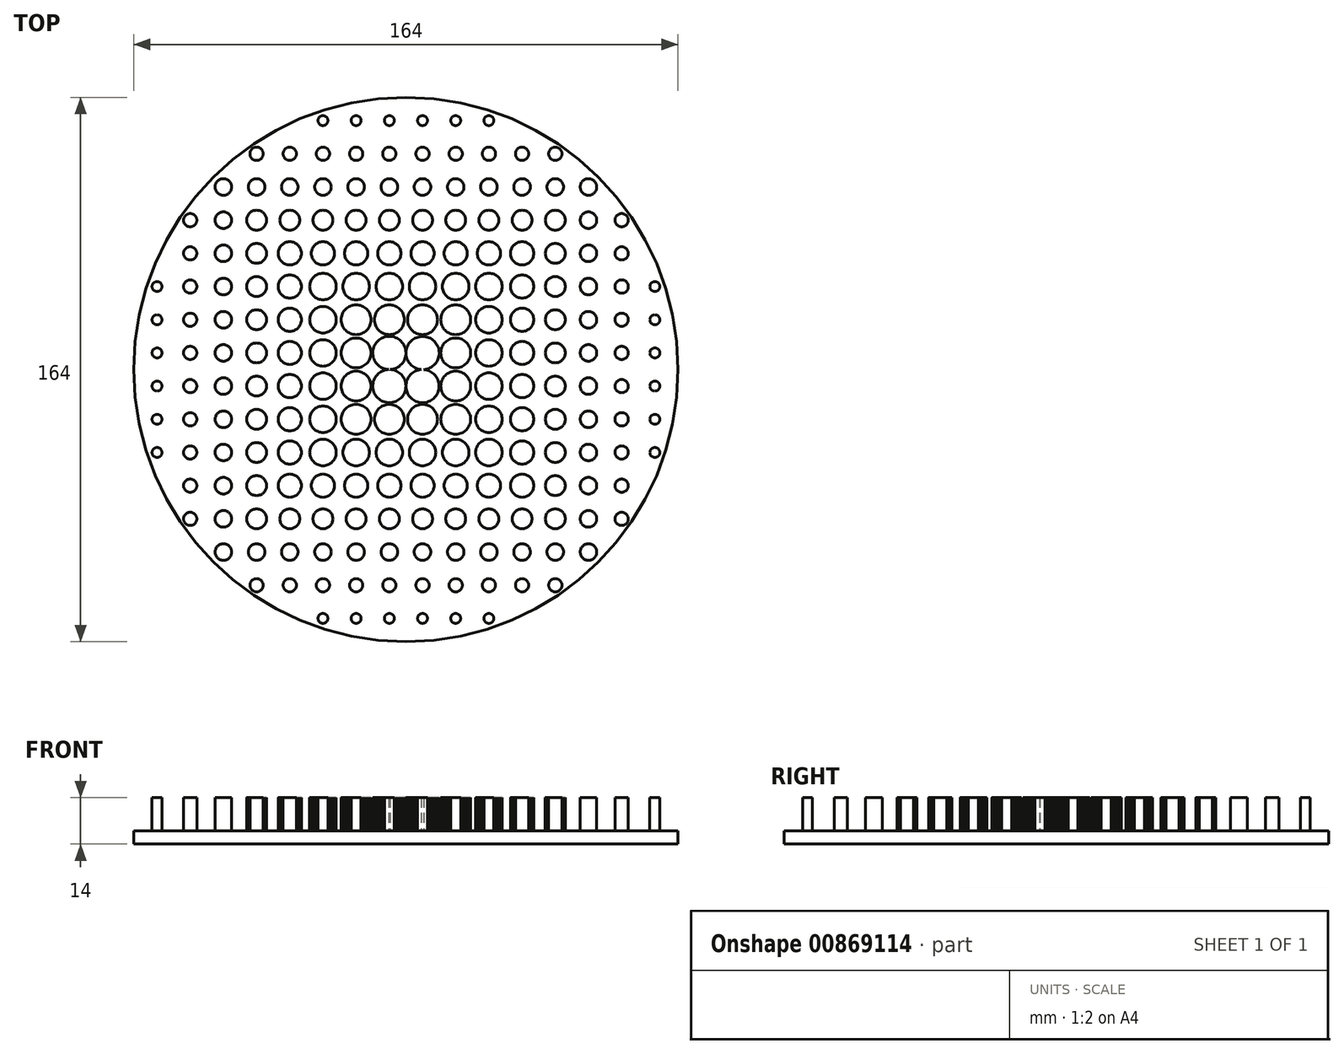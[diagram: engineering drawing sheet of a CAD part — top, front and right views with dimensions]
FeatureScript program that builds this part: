
annotation { "Feature Type Name" : "Feature", "Feature Type Description" : "" }
export const myFeature = defineFeature(function(context is Context, id is Id, definition is map)
    precondition{}
    {
        {
            var Q0;
            Q0=qCreatedBy(makeId("Top.planeOp"),FACE);
            var sketch = newSketch(context, id + "F0", { "sketchPlane" : qUnion([Q0])});
            skCircle(sketch, "E0", {"center": v(0, 0) * mm, "radius": 82 * mm});
            skSolve(sketch);
        }
        {
            var Q0;
            Q0=qSketchRegion(id+"F0",true);
            extrude(context, id + "F1", {"entities" : qUnion([Q0]), "oppositeDirection" : true, "depth" : 4 * mm, "offsetDistance" : 25 * mm});
        }
        {
            var Q0;
            Q0=makeQuery(id+"F1.opExtrude","CAP_FACE",FACE,{"disambiguationData":[OSD([sQuery(id+"F0.wireOp",EDGE,"E0")])],"isStart":true});
            var sketch = newSketch(context, id + "F2", { "sketchPlane" : qUnion([Q0])});
            skCircle(sketch, "E1", {"center": v(-5, 5) * mm, "radius": 5 * mm});
            skCircle(sketch, "E2", {"center": v(-5, 15) * mm, "radius": 4.5 * mm});
            skCircle(sketch, "E3.MirrorC", {"center": v(15, -5) * mm, "radius": 4.5 * mm});
            skCircle(sketch, "E4", {"center": v(5, 15) * mm, "radius": 4.5 * mm});
            skCircle(sketch, "E5.MirrorC", {"center": v(15, 5) * mm, "radius": 4.5 * mm});
            skCircle(sketch, "E6", {"center": v(15, 15) * mm, "radius": 4.5 * mm});
            skCircle(sketch, "E7", {"center": v(-15, 5) * mm, "radius": 4.5 * mm});
            skCircle(sketch, "E8", {"center": v(-15, -5) * mm, "radius": 4.5 * mm});
            skCircle(sketch, "E9.MirrorC", {"center": v(5, -15) * mm, "radius": 4.5 * mm});
            skCircle(sketch, "E10.MirrorC", {"center": v(-5, -15) * mm, "radius": 4.5 * mm});
            skCircle(sketch, "E11", {"center": v(-15, 15) * mm, "radius": 4.5 * mm});
            skCircle(sketch, "E12.MirrorC", {"center": v(15, -15) * mm, "radius": 4.5 * mm});
            skCircle(sketch, "E13", {"center": v(-15, -15) * mm, "radius": 4.5 * mm});
            skCircle(sketch, "E14", {"center": v(-15, 25) * mm, "radius": 4 * mm});
            skCircle(sketch, "E15.1.0.0", {"center": v(-5, 25) * mm, "radius": 4 * mm});
            skCircle(sketch, "E15.2.0.0", {"center": v(5, 25) * mm, "radius": 4 * mm});
            skCircle(sketch, "E15.3.0.0", {"center": v(15, 25) * mm, "radius": 4 * mm});
            skCircle(sketch, "E15.4.0.0", {"center": v(25, 25) * mm, "radius": 4 * mm});
            skLineSegment(sketch, "E15.direction1", {"start": v(-15, 25) * mm, "end": v(-5, 25) * mm, "construction": true});
            skCircle(sketch, "E16", {"center": v(-25, 25) * mm, "radius": 4 * mm});
            skCircle(sketch, "E17.MirrorC", {"center": v(25, 15) * mm, "radius": 4 * mm});
            skCircle(sketch, "E18.MirrorC", {"center": v(25, 5) * mm, "radius": 4 * mm});
            skCircle(sketch, "E19.MirrorC", {"center": v(25, -5) * mm, "radius": 4 * mm});
            skCircle(sketch, "E20.MirrorC", {"center": v(25, -15) * mm, "radius": 4 * mm});
            skCircle(sketch, "E21.MirrorC", {"center": v(25, -25) * mm, "radius": 4 * mm});
            skCircle(sketch, "E22.1.0.0", {"center": v(15, -25) * mm, "radius": 4 * mm});
            skCircle(sketch, "E22.2.0.0", {"center": v(5, -25) * mm, "radius": 4 * mm});
            skCircle(sketch, "E22.3.0.0", {"center": v(-5, -25) * mm, "radius": 4 * mm});
            skCircle(sketch, "E22.4.0.0", {"center": v(-15, -25) * mm, "radius": 4 * mm});
            skCircle(sketch, "E22.5.0.0", {"center": v(-25, -25) * mm, "radius": 4 * mm});
            skLineSegment(sketch, "E22.direction1", {"start": v(25, -25) * mm, "end": v(15, -25) * mm, "construction": true});
            skCircle(sketch, "E23.MirrorC", {"center": v(-25, 15) * mm, "radius": 4 * mm});
            skCircle(sketch, "E24.MirrorC", {"center": v(-25, 5) * mm, "radius": 4 * mm});
            skCircle(sketch, "E25.MirrorC", {"center": v(-25, -5) * mm, "radius": 4 * mm});
            skCircle(sketch, "E26.MirrorC", {"center": v(-25, -15) * mm, "radius": 4 * mm});
            skCircle(sketch, "E27", {"center": v(-25, 35) * mm, "radius": 3.5 * mm});
            skCircle(sketch, "E28.1.0.0", {"center": v(-15, 35) * mm, "radius": 3.5 * mm});
            skCircle(sketch, "E28.2.0.0", {"center": v(-5, 35) * mm, "radius": 3.5 * mm});
            skCircle(sketch, "E28.3.0.0", {"center": v(5, 35) * mm, "radius": 3.5 * mm});
            skCircle(sketch, "E28.4.0.0", {"center": v(15, 35) * mm, "radius": 3.5 * mm});
            skCircle(sketch, "E28.5.0.0", {"center": v(25, 35) * mm, "radius": 3.5 * mm});
            skCircle(sketch, "E28.6.0.0", {"center": v(35, 35) * mm, "radius": 3.5 * mm});
            skLineSegment(sketch, "E28.direction1", {"start": v(-25, 35) * mm, "end": v(-15, 35) * mm, "construction": true});
            skCircle(sketch, "E29.MirrorC", {"center": v(35, -15) * mm, "radius": 3.5 * mm});
            skCircle(sketch, "E30.MirrorC", {"center": v(35, -5) * mm, "radius": 3.5 * mm});
            skCircle(sketch, "E31.MirrorC", {"center": v(35, 5) * mm, "radius": 3.5 * mm});
            skCircle(sketch, "E32.MirrorC", {"center": v(35, 15) * mm, "radius": 3.5 * mm});
            skCircle(sketch, "E33.MirrorC", {"center": v(35, 25) * mm, "radius": 3.5 * mm});
            skCircle(sketch, "E34.MirrorC", {"center": v(35, -25) * mm, "radius": 3.5 * mm});
            skCircle(sketch, "E35.MirrorC", {"center": v(35, -35) * mm, "radius": 3.5 * mm});
            skCircle(sketch, "E36.1.0.0", {"center": v(25, -35) * mm, "radius": 3.5 * mm});
            skCircle(sketch, "E36.2.0.0", {"center": v(15, -35) * mm, "radius": 3.5 * mm});
            skCircle(sketch, "E36.3.0.0", {"center": v(5, -35) * mm, "radius": 3.5 * mm});
            skCircle(sketch, "E36.4.0.0", {"center": v(-5, -35) * mm, "radius": 3.5 * mm});
            skCircle(sketch, "E36.5.0.0", {"center": v(-15, -35) * mm, "radius": 3.5 * mm});
            skCircle(sketch, "E36.6.0.0", {"center": v(-25, -35) * mm, "radius": 3.5 * mm});
            skCircle(sketch, "E36.7.0.0", {"center": v(-35, -35) * mm, "radius": 3.5 * mm});
            skLineSegment(sketch, "E36.direction1", {"start": v(35, -35) * mm, "end": v(25, -35) * mm, "construction": true});
            skCircle(sketch, "E37.MirrorC", {"center": v(-35, -25) * mm, "radius": 3.5 * mm});
            skCircle(sketch, "E38.MirrorC", {"center": v(-35, -15) * mm, "radius": 3.5 * mm});
            skCircle(sketch, "E39.MirrorC", {"center": v(-35, -5) * mm, "radius": 3.5 * mm});
            skCircle(sketch, "E40.MirrorC", {"center": v(-35, 5) * mm, "radius": 3.5 * mm});
            skCircle(sketch, "E41.MirrorC", {"center": v(-35, 15) * mm, "radius": 3.5 * mm});
            skCircle(sketch, "E42.MirrorC", {"center": v(-35, 25) * mm, "radius": 3.5 * mm});
            skCircle(sketch, "E43.MirrorC", {"center": v(-35, 35) * mm, "radius": 3.5 * mm});
            skCircle(sketch, "E44", {"center": v(-35, 45) * mm, "radius": 3 * mm});
            skCircle(sketch, "E45.1.0.0", {"center": v(-25, 45) * mm, "radius": 3 * mm});
            skCircle(sketch, "E45.2.0.0", {"center": v(-15, 45) * mm, "radius": 3 * mm});
            skCircle(sketch, "E45.3.0.0", {"center": v(-5, 45) * mm, "radius": 3 * mm});
            skCircle(sketch, "E45.4.0.0", {"center": v(5, 45) * mm, "radius": 3 * mm});
            skCircle(sketch, "E45.5.0.0", {"center": v(15, 45) * mm, "radius": 3 * mm});
            skCircle(sketch, "E45.6.0.0", {"center": v(25, 45) * mm, "radius": 3 * mm});
            skCircle(sketch, "E45.7.0.0", {"center": v(35, 45) * mm, "radius": 3 * mm});
            skCircle(sketch, "E45.8.0.0", {"center": v(45, 45) * mm, "radius": 3 * mm});
            skLineSegment(sketch, "E45.direction1", {"start": v(-35, 45) * mm, "end": v(-25, 45) * mm, "construction": true});
            skCircle(sketch, "E46.MirrorC", {"center": v(45, -25) * mm, "radius": 3 * mm});
            skCircle(sketch, "E47.MirrorC", {"center": v(45, -35) * mm, "radius": 3 * mm});
            skCircle(sketch, "E48.MirrorC", {"center": v(45, -15) * mm, "radius": 3 * mm});
            skCircle(sketch, "E49.MirrorC", {"center": v(45, -5) * mm, "radius": 3 * mm});
            skCircle(sketch, "E50.MirrorC", {"center": v(45, 5) * mm, "radius": 3 * mm});
            skCircle(sketch, "E51.MirrorC", {"center": v(45, 15) * mm, "radius": 3 * mm});
            skCircle(sketch, "E52.MirrorC", {"center": v(45, 25) * mm, "radius": 3 * mm});
            skCircle(sketch, "E53.MirrorC", {"center": v(45, 35) * mm, "radius": 3 * mm});
            skCircle(sketch, "E54.MirrorC", {"center": v(45, -45) * mm, "radius": 3 * mm});
            skCircle(sketch, "E55.1.0.0", {"center": v(35, -45) * mm, "radius": 3 * mm});
            skCircle(sketch, "E55.2.0.0", {"center": v(25, -45) * mm, "radius": 3 * mm});
            skCircle(sketch, "E55.3.0.0", {"center": v(15, -45) * mm, "radius": 3 * mm});
            skCircle(sketch, "E55.4.0.0", {"center": v(5, -45) * mm, "radius": 3 * mm});
            skCircle(sketch, "E55.5.0.0", {"center": v(-5, -45) * mm, "radius": 3 * mm});
            skCircle(sketch, "E55.6.0.0", {"center": v(-15, -45) * mm, "radius": 3 * mm});
            skCircle(sketch, "E55.7.0.0", {"center": v(-25, -45) * mm, "radius": 3 * mm});
            skCircle(sketch, "E55.8.0.0", {"center": v(-35, -45) * mm, "radius": 3 * mm});
            skCircle(sketch, "E55.9.0.0", {"center": v(-45, -45) * mm, "radius": 3 * mm});
            skLineSegment(sketch, "E55.direction1", {"start": v(45, -45) * mm, "end": v(35, -45) * mm, "construction": true});
            skCircle(sketch, "E56.MirrorC", {"center": v(-45, -35) * mm, "radius": 3 * mm});
            skCircle(sketch, "E57.MirrorC", {"center": v(-45, -25) * mm, "radius": 3 * mm});
            skCircle(sketch, "E58.MirrorC", {"center": v(-45, -15) * mm, "radius": 3 * mm});
            skCircle(sketch, "E59.MirrorC", {"center": v(-45, -5) * mm, "radius": 3 * mm});
            skCircle(sketch, "E60.MirrorC", {"center": v(-45, 5) * mm, "radius": 3 * mm});
            skCircle(sketch, "E61.MirrorC", {"center": v(-45, 15) * mm, "radius": 3 * mm});
            skCircle(sketch, "E62.MirrorC", {"center": v(-45, 25) * mm, "radius": 3 * mm});
            skCircle(sketch, "E63.MirrorC", {"center": v(-45, 35) * mm, "radius": 3 * mm});
            skCircle(sketch, "E64.MirrorC", {"center": v(-45, 45) * mm, "radius": 3 * mm});
            skCircle(sketch, "E65", {"center": v(-45, 55) * mm, "radius": 2.5 * mm});
            skCircle(sketch, "E66.1.0.0", {"center": v(-35, 55) * mm, "radius": 2.5 * mm});
            skCircle(sketch, "E66.2.0.0", {"center": v(-25, 55) * mm, "radius": 2.5 * mm});
            skCircle(sketch, "E66.3.0.0", {"center": v(-15, 55) * mm, "radius": 2.5 * mm});
            skCircle(sketch, "E66.4.0.0", {"center": v(-5, 55) * mm, "radius": 2.5 * mm});
            skCircle(sketch, "E66.5.0.0", {"center": v(5, 55) * mm, "radius": 2.5 * mm});
            skCircle(sketch, "E66.6.0.0", {"center": v(15, 55) * mm, "radius": 2.5 * mm});
            skCircle(sketch, "E66.7.0.0", {"center": v(25, 55) * mm, "radius": 2.5 * mm});
            skCircle(sketch, "E66.8.0.0", {"center": v(35, 55) * mm, "radius": 2.5 * mm});
            skCircle(sketch, "E66.9.0.0", {"center": v(45, 55) * mm, "radius": 2.5 * mm});
            skCircle(sketch, "E66.10.0.0", {"center": v(55, 55) * mm, "radius": 2.5 * mm});
            skLineSegment(sketch, "E66.direction1", {"start": v(-45, 55) * mm, "end": v(-35, 55) * mm, "construction": true});
            skCircle(sketch, "E67.MirrorC", {"center": v(55, -35) * mm, "radius": 2.5 * mm});
            skCircle(sketch, "E68.MirrorC", {"center": v(55, -25) * mm, "radius": 2.5 * mm});
            skCircle(sketch, "E69.MirrorC", {"center": v(55, -45) * mm, "radius": 2.5 * mm});
            skCircle(sketch, "E70.MirrorC", {"center": v(55, -15) * mm, "radius": 2.5 * mm});
            skCircle(sketch, "E71.MirrorC", {"center": v(55, -5) * mm, "radius": 2.5 * mm});
            skCircle(sketch, "E72.MirrorC", {"center": v(55, 5) * mm, "radius": 2.5 * mm});
            skCircle(sketch, "E73.MirrorC", {"center": v(55, 15) * mm, "radius": 2.5 * mm});
            skCircle(sketch, "E74.MirrorC", {"center": v(55, 25) * mm, "radius": 2.5 * mm});
            skCircle(sketch, "E75.MirrorC", {"center": v(55, 35) * mm, "radius": 2.5 * mm});
            skCircle(sketch, "E76.MirrorC", {"center": v(55, 45) * mm, "radius": 2.5 * mm});
            skCircle(sketch, "E77", {"center": v(55, -55) * mm, "radius": 2.5 * mm});
            skCircle(sketch, "E78.1.0.0", {"center": v(45, -55) * mm, "radius": 2.5 * mm});
            skCircle(sketch, "E78.2.0.0", {"center": v(35, -55) * mm, "radius": 2.5 * mm});
            skCircle(sketch, "E78.3.0.0", {"center": v(25, -55) * mm, "radius": 2.5 * mm});
            skCircle(sketch, "E78.4.0.0", {"center": v(15, -55) * mm, "radius": 2.5 * mm});
            skCircle(sketch, "E78.5.0.0", {"center": v(5, -55) * mm, "radius": 2.5 * mm});
            skCircle(sketch, "E78.6.0.0", {"center": v(-5, -55) * mm, "radius": 2.5 * mm});
            skCircle(sketch, "E78.7.0.0", {"center": v(-15, -55) * mm, "radius": 2.5 * mm});
            skCircle(sketch, "E78.8.0.0", {"center": v(-25, -55) * mm, "radius": 2.5 * mm});
            skCircle(sketch, "E78.9.0.0", {"center": v(-35, -55) * mm, "radius": 2.5 * mm});
            skCircle(sketch, "E78.10.0.0", {"center": v(-45, -55) * mm, "radius": 2.5 * mm});
            skCircle(sketch, "E78.11.0.0", {"center": v(-55, -55) * mm, "radius": 2.5 * mm});
            skLineSegment(sketch, "E78.direction1", {"start": v(55, -55) * mm, "end": v(45, -55) * mm, "construction": true});
            skCircle(sketch, "E79.MirrorC", {"center": v(-55, -45) * mm, "radius": 2.5 * mm});
            skCircle(sketch, "E80.MirrorC", {"center": v(-55, -35) * mm, "radius": 2.5 * mm});
            skCircle(sketch, "E81.MirrorC", {"center": v(-55, -25) * mm, "radius": 2.5 * mm});
            skCircle(sketch, "E82.MirrorC", {"center": v(-55, -15) * mm, "radius": 2.5 * mm});
            skCircle(sketch, "E83.MirrorC", {"center": v(-55, 5) * mm, "radius": 2.5 * mm});
            skCircle(sketch, "E84.MirrorC", {"center": v(-55, -5) * mm, "radius": 2.5 * mm});
            skCircle(sketch, "E85.MirrorC", {"center": v(-55, 15) * mm, "radius": 2.5 * mm});
            skCircle(sketch, "E86.MirrorC", {"center": v(-55, 25) * mm, "radius": 2.5 * mm});
            skCircle(sketch, "E87.MirrorC", {"center": v(-55, 35) * mm, "radius": 2.5 * mm});
            skCircle(sketch, "E88.MirrorC", {"center": v(-55, 45) * mm, "radius": 2.5 * mm});
            skCircle(sketch, "E89.MirrorC", {"center": v(-55, 55) * mm, "radius": 2.5 * mm});
            skCircle(sketch, "E90", {"center": v(-65, -45) * mm, "radius": 2 * mm});
            skCircle(sketch, "E91.MirrorC", {"center": v(-45, -65) * mm, "radius": 2 * mm});
            skCircle(sketch, "E92.1.0.0", {"center": v(-35, -65) * mm, "radius": 2 * mm});
            skCircle(sketch, "E92.2.0.0", {"center": v(-25, -65) * mm, "radius": 2 * mm});
            skCircle(sketch, "E92.3.0.0", {"center": v(-15, -65) * mm, "radius": 2 * mm});
            skCircle(sketch, "E92.4.0.0", {"center": v(-5, -65) * mm, "radius": 2 * mm});
            skCircle(sketch, "E92.5.0.0", {"center": v(5, -65) * mm, "radius": 2 * mm});
            skCircle(sketch, "E92.6.0.0", {"center": v(15, -65) * mm, "radius": 2 * mm});
            skCircle(sketch, "E92.7.0.0", {"center": v(25, -65) * mm, "radius": 2 * mm});
            skCircle(sketch, "E92.8.0.0", {"center": v(35, -65) * mm, "radius": 2 * mm});
            skCircle(sketch, "E92.9.0.0", {"center": v(45, -65) * mm, "radius": 2 * mm});
            skLineSegment(sketch, "E92.direction1", {"start": v(-45, -65) * mm, "end": v(-35, -65) * mm, "construction": true});
            skCircle(sketch, "E93.MirrorC", {"center": v(-65, -35) * mm, "radius": 2 * mm});
            skCircle(sketch, "E94.MirrorC", {"center": v(-65, -25) * mm, "radius": 2 * mm});
            skCircle(sketch, "E95.MirrorC", {"center": v(-65, -15) * mm, "radius": 2 * mm});
            skCircle(sketch, "E96.MirrorC", {"center": v(-65, -5) * mm, "radius": 2 * mm});
            skCircle(sketch, "E97.MirrorC", {"center": v(-65, 5) * mm, "radius": 2 * mm});
            skCircle(sketch, "E98.MirrorC", {"center": v(-65, 15) * mm, "radius": 2 * mm});
            skCircle(sketch, "E99.MirrorC", {"center": v(-65, 25) * mm, "radius": 2 * mm});
            skCircle(sketch, "E100.MirrorC", {"center": v(-65, 35) * mm, "radius": 2 * mm});
            skCircle(sketch, "E101.MirrorC", {"center": v(-65, 45) * mm, "radius": 2 * mm});
            skCircle(sketch, "E102", {"center": v(-45, 65) * mm, "radius": 2 * mm});
            skCircle(sketch, "E103.1.0.0", {"center": v(-35, 65) * mm, "radius": 2 * mm});
            skCircle(sketch, "E103.2.0.0", {"center": v(-25, 65) * mm, "radius": 2 * mm});
            skCircle(sketch, "E103.3.0.0", {"center": v(-15, 65) * mm, "radius": 2 * mm});
            skCircle(sketch, "E103.4.0.0", {"center": v(-5, 65) * mm, "radius": 2 * mm});
            skCircle(sketch, "E103.5.0.0", {"center": v(5, 65) * mm, "radius": 2 * mm});
            skCircle(sketch, "E103.6.0.0", {"center": v(15, 65) * mm, "radius": 2 * mm});
            skCircle(sketch, "E103.7.0.0", {"center": v(25, 65) * mm, "radius": 2 * mm});
            skCircle(sketch, "E103.8.0.0", {"center": v(35, 65) * mm, "radius": 2 * mm});
            skCircle(sketch, "E103.9.0.0", {"center": v(45, 65) * mm, "radius": 2 * mm});
            skLineSegment(sketch, "E103.direction1", {"start": v(-45, 65) * mm, "end": v(-35, 65) * mm, "construction": true});
            skCircle(sketch, "E104.MirrorC", {"center": v(65, -45) * mm, "radius": 2 * mm});
            skCircle(sketch, "E105.MirrorC", {"center": v(65, -35) * mm, "radius": 2 * mm});
            skCircle(sketch, "E106.MirrorC", {"center": v(65, -25) * mm, "radius": 2 * mm});
            skCircle(sketch, "E107.MirrorC", {"center": v(65, -15) * mm, "radius": 2 * mm});
            skCircle(sketch, "E108.MirrorC", {"center": v(65, -5) * mm, "radius": 2 * mm});
            skCircle(sketch, "E109.MirrorC", {"center": v(65, 5) * mm, "radius": 2 * mm});
            skCircle(sketch, "E110.MirrorC", {"center": v(65, 15) * mm, "radius": 2 * mm});
            skCircle(sketch, "E111.MirrorC", {"center": v(65, 25) * mm, "radius": 2 * mm});
            skCircle(sketch, "E112.MirrorC", {"center": v(65, 35) * mm, "radius": 2 * mm});
            skCircle(sketch, "E113.MirrorC", {"center": v(65, 45) * mm, "radius": 2 * mm});
            skCircle(sketch, "E114", {"center": v(-25, 75) * mm, "radius": 1.5 * mm});
            skCircle(sketch, "E115.1.0.0", {"center": v(-15, 75) * mm, "radius": 1.5 * mm});
            skCircle(sketch, "E115.2.0.0", {"center": v(-5, 75) * mm, "radius": 1.5 * mm});
            skCircle(sketch, "E115.3.0.0", {"center": v(5, 75) * mm, "radius": 1.5 * mm});
            skCircle(sketch, "E115.4.0.0", {"center": v(15, 75) * mm, "radius": 1.5 * mm});
            skCircle(sketch, "E115.5.0.0", {"center": v(25, 75) * mm, "radius": 1.5 * mm});
            skLineSegment(sketch, "E115.direction1", {"start": v(-25, 75) * mm, "end": v(-15, 75) * mm, "construction": true});
            skCircle(sketch, "E116.MirrorC", {"center": v(75, -25) * mm, "radius": 1.5 * mm});
            skCircle(sketch, "E117.MirrorC", {"center": v(75, -15) * mm, "radius": 1.5 * mm});
            skCircle(sketch, "E118.MirrorC", {"center": v(75, -5) * mm, "radius": 1.5 * mm});
            skCircle(sketch, "E119.MirrorC", {"center": v(75, 5) * mm, "radius": 1.5 * mm});
            skCircle(sketch, "E120.MirrorC", {"center": v(75, 15) * mm, "radius": 1.5 * mm});
            skCircle(sketch, "E121", {"center": v(25, -75) * mm, "radius": 1.5 * mm});
            skCircle(sketch, "E122.1.0.0", {"center": v(15, -75) * mm, "radius": 1.5 * mm});
            skCircle(sketch, "E122.2.0.0", {"center": v(5, -75) * mm, "radius": 1.5 * mm});
            skCircle(sketch, "E122.3.0.0", {"center": v(-5, -75) * mm, "radius": 1.5 * mm});
            skCircle(sketch, "E122.4.0.0", {"center": v(-15, -75) * mm, "radius": 1.5 * mm});
            skCircle(sketch, "E122.5.0.0", {"center": v(-25, -75) * mm, "radius": 1.5 * mm});
            skLineSegment(sketch, "E122.direction1", {"start": v(25, -75) * mm, "end": v(15, -75) * mm, "construction": true});
            skCircle(sketch, "E123.MirrorC", {"center": v(-75, -25) * mm, "radius": 1.5 * mm});
            skCircle(sketch, "E124.MirrorC", {"center": v(-75, -15) * mm, "radius": 1.5 * mm});
            skCircle(sketch, "E125.MirrorC", {"center": v(-75, -5) * mm, "radius": 1.5 * mm});
            skCircle(sketch, "E126.MirrorC", {"center": v(-75, 5) * mm, "radius": 1.5 * mm});
            skCircle(sketch, "E127.MirrorC", {"center": v(-75, 15) * mm, "radius": 1.5 * mm});
            skCircle(sketch, "E128.MirrorC", {"center": v(-75, 25) * mm, "radius": 1.5 * mm});
            skCircle(sketch, "E129.MirrorC", {"center": v(75, 25) * mm, "radius": 1.5 * mm});
            skSolve(sketch);
        }
        {
            var Q0;
            Q0 = qSketchRegion(id + "F2", true);
            var Q1;
            Q1 = qConstructionFilter(qBodyType(qCreatedBy(id + "F2" ,EDGE), BodyType.WIRE), ConstructionObject.NO);
            extrude(context, id + "F3", {"entities" : qUnion([Q0]), "operationType" : NewBodyOperationType.ADD, "surfaceEntities" : qUnion([Q1]), "depth" : 10 * mm, "offsetDistance" : 25 * mm});
        }
        {
            var Q0;
            Q0=makeQuery(id+"F1.opExtrude","CAP_FACE",FACE,{"disambiguationData":[OSD([sQuery(id+"F0.wireOp",EDGE,"E0")])],"isStart":true});
            var sketch = newSketch(context, id + "F4", { "sketchPlane" : qUnion([Q0])});
            skCircle(sketch, "E130", {"center": v(5.03, 4.97) * mm, "radius": 5 * mm});
            skSolve(sketch);
        }
        {
            var Q0;
            Q0 = qSketchRegion(id + "F4", true);
            extrude(context, id + "F5", {"entities" : qUnion([Q0]), "operationType" : NewBodyOperationType.ADD, "depth" : 10 * mm, "offsetDistance" : 25 * mm});
        }
        {
            var Q0;
            Q0=makeQuery(id+"F1.opExtrude","CAP_FACE",FACE,{"disambiguationData":[OSD([sQuery(id+"F0.wireOp",EDGE,"E0")])],"isStart":true});
            var sketch = newSketch(context, id + "F6", { "sketchPlane" : qUnion([Q0])});
            skCircle(sketch, "E131", {"center": v(-5, -4.99) * mm, "radius": 5 * mm});
            skPoint(sketch, "E132", {"position": v(-5, 0.01) * mm});
            skPoint(sketch, "E133", {"position": v(0, -5) * mm});
            skLineSegment(sketch, "E134", {"start": v(0, -5) * mm, "end": v(0, 0) * mm});
            skSolve(sketch);
        }
        {
            var Q0;
            Q0 = qSketchRegion(id + "F6", true);
            extrude(context, id + "F7", {"entities" : qUnion([Q0]), "operationType" : NewBodyOperationType.ADD, "depth" : 10 * mm, "offsetDistance" : 25 * mm});
        }
        {
            var Q0;
            Q0=makeQuery(id+"F1.opExtrude","CAP_FACE",FACE,{"disambiguationData":[OSD([sQuery(id+"F0.wireOp",EDGE,"E0")])],"isStart":true});
            var sketch = newSketch(context, id + "F8", { "sketchPlane" : qUnion([Q0])});
            skCircle(sketch, "E135", {"center": v(5, -5) * mm, "radius": 5 * mm});
            skPoint(sketch, "E136", {"position": v(5.08, 0) * mm});
            skPoint(sketch, "E137", {"position": v(0, -4.92) * mm});
            skLineSegment(sketch, "E138", {"start": v(0, -4.92) * mm, "end": v(5, -5) * mm});
            skLineSegment(sketch, "E139", {"start": v(5.08, 0) * mm, "end": v(5, -5) * mm});
            skSolve(sketch);
        }
        {
            var Q0;
            Q0 = qSketchRegion(id + "F8", true);
            extrude(context, id + "F9", {"entities" : qUnion([Q0]), "operationType" : NewBodyOperationType.ADD, "depth" : 10 * mm, "offsetDistance" : 25 * mm});
        }
    });
